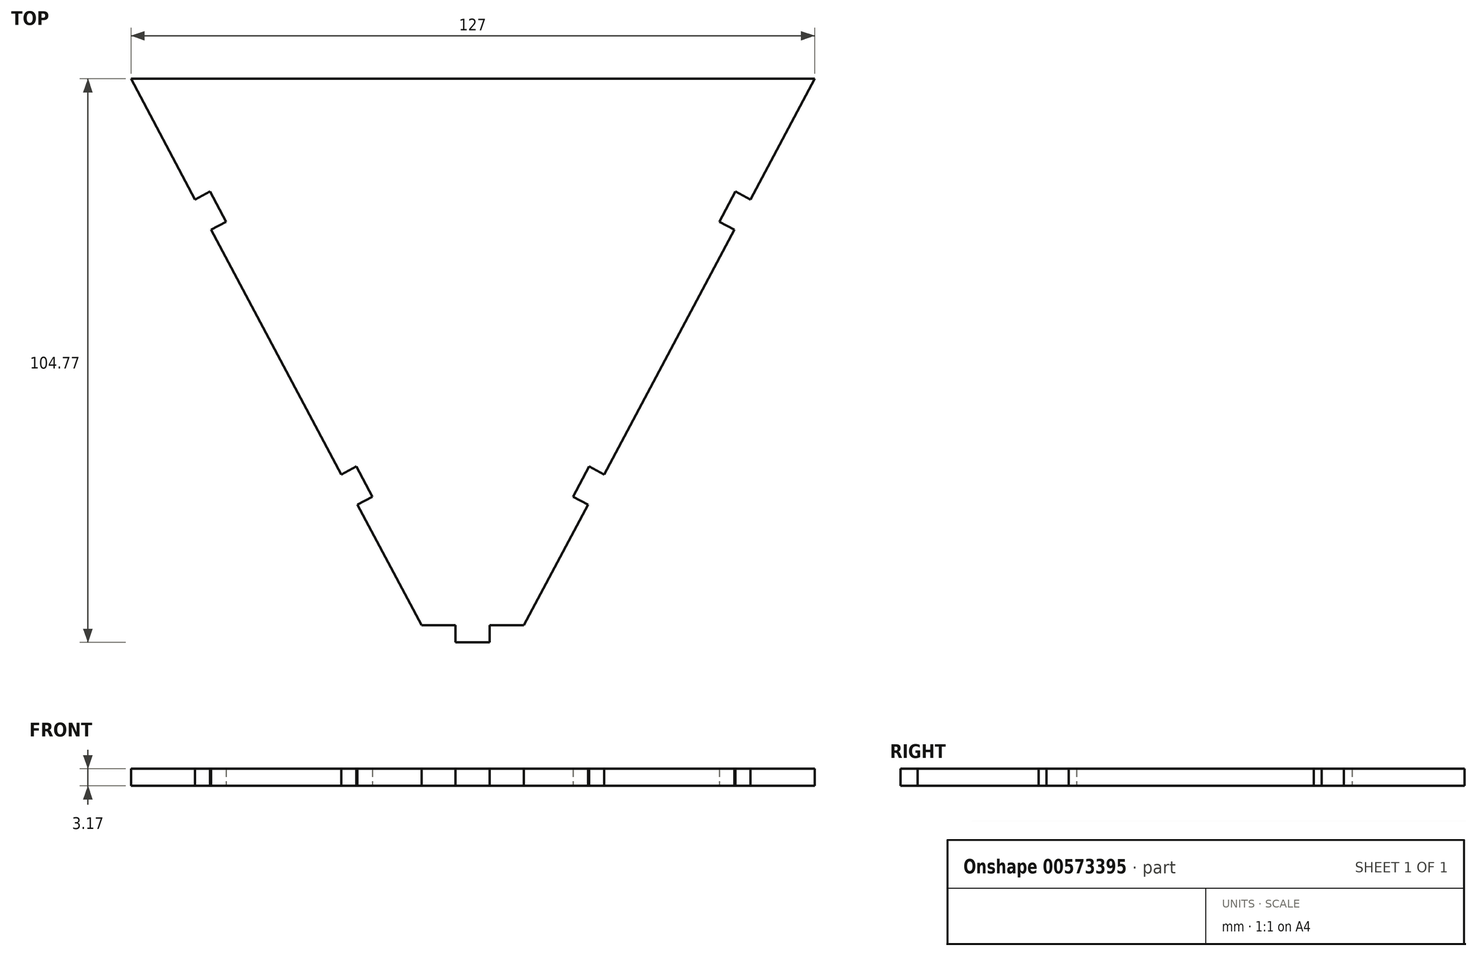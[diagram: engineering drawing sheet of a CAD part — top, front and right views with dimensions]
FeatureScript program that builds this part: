
annotation { "Feature Type Name" : "Feature", "Feature Type Description" : "" }
export const myFeature = defineFeature(function(context is Context, id is Id, definition is map)
    precondition{}
    {
        {
            var Q0;
            Q0=qCreatedBy(makeId("Top.planeOp"),FACE);
            var sketch = newSketch(context, id + "F0", { "sketchPlane" : qUnion([Q0])});
            skLineSegment(sketch, "E0", {"start": v(0, 101.6) * mm, "end": v(127, 101.6) * mm});
            skLineSegment(sketch, "E1", {"start": v(0, 101.6) * mm, "end": v(11.92, 79.17) * mm});
            skLineSegment(sketch, "E2", {"start": v(11.92, 79.17) * mm, "end": v(14.72, 80.66) * mm});
            skLineSegment(sketch, "E3", {"start": v(14.72, 80.66) * mm, "end": v(17.7, 75.05) * mm});
            skLineSegment(sketch, "E4", {"start": v(17.7, 75.05) * mm, "end": v(14.9, 73.56) * mm});
            skLineSegment(sketch, "E5", {"start": v(53.98, 0) * mm, "end": v(42.06, 22.43) * mm});
            skLineSegment(sketch, "E6", {"start": v(42.06, 22.43) * mm, "end": v(44.86, 23.92) * mm});
            skLineSegment(sketch, "E7", {"start": v(44.86, 23.92) * mm, "end": v(41.88, 29.53) * mm});
            skLineSegment(sketch, "E8", {"start": v(41.88, 29.53) * mm, "end": v(39.08, 28.04) * mm});
            skLineSegment(sketch, "E9", {"start": v(39.08, 28.04) * mm, "end": v(14.9, 73.56) * mm});
            skLineSegment(sketch, "E10.MirrorCS", {"start": v(84.94, 22.43) * mm, "end": v(82.14, 23.92) * mm});
            skLineSegment(sketch, "E11.MirrorCS", {"start": v(73.03, 0) * mm, "end": v(84.94, 22.43) * mm});
            skLineSegment(sketch, "E12.MirrorCS", {"start": v(87.92, 28.04) * mm, "end": v(112.1, 73.56) * mm});
            skLineSegment(sketch, "E13.MirrorCS", {"start": v(115.08, 79.17) * mm, "end": v(112.28, 80.66) * mm});
            skLineSegment(sketch, "E14.MirrorCS", {"start": v(85.12, 29.53) * mm, "end": v(87.92, 28.04) * mm});
            skLineSegment(sketch, "E15.MirrorCS", {"start": v(127, 101.6) * mm, "end": v(115.08, 79.17) * mm});
            skLineSegment(sketch, "E16.MirrorCS", {"start": v(109.3, 75.05) * mm, "end": v(112.1, 73.56) * mm});
            skLineSegment(sketch, "E17.MirrorCS", {"start": v(112.28, 80.66) * mm, "end": v(109.3, 75.05) * mm});
            skLineSegment(sketch, "E18.MirrorCS", {"start": v(82.14, 23.92) * mm, "end": v(85.12, 29.53) * mm});
            skLineSegment(sketch, "E19", {"start": v(63.5, -3.18) * mm, "end": v(60.33, -3.18) * mm});
            skLineSegment(sketch, "E20", {"start": v(60.33, -3.18) * mm, "end": v(60.33, 0) * mm});
            skLineSegment(sketch, "E21", {"start": v(63.5, -3.18) * mm, "end": v(66.67, -3.18) * mm});
            skLineSegment(sketch, "E22", {"start": v(66.67, -3.18) * mm, "end": v(66.67, 0) * mm});
            skLineSegment(sketch, "E23", {"start": v(53.98, 0) * mm, "end": v(60.33, 0) * mm});
            skLineSegment(sketch, "E24", {"start": v(66.67, 0) * mm, "end": v(73.03, 0) * mm});
            skSolve(sketch);
        }
        {
            var Q0;
            Q0=makeQuery(id+"F0.imprint","IMPRINT",FACE,{"disambiguationData":[TD([[makeQuery(id+"F0.imprint","IMPRINT",EDGE,{"derivedFrom":sQuery(id+"F0.wireOp",EDGE,"E0")}),-1.0]])]});
            extrude(context, id + "F1", {"entities" : qUnion([Q0]), "depth" : 3.17 * mm, "offsetDistance" : 25.4 * mm});
        }
    });
